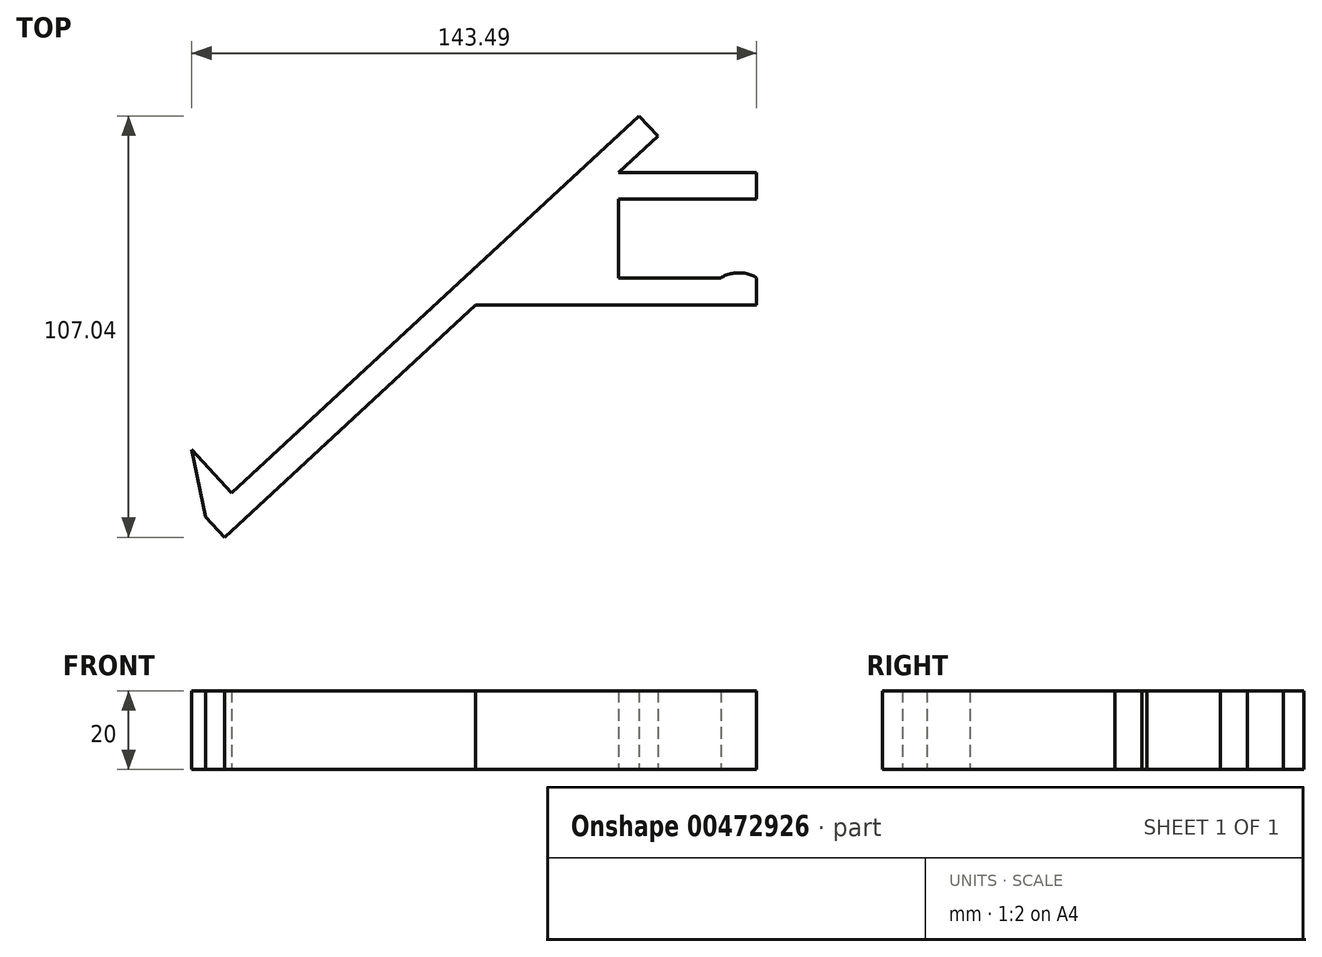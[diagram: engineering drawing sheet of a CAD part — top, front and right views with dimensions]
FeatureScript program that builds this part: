
annotation { "Feature Type Name" : "Feature", "Feature Type Description" : "" }
export const myFeature = defineFeature(function(context is Context, id is Id, definition is map)
    precondition{}
    {
        {
            var Q0;
            Q0=qCreatedBy(makeId("Top.planeOp"),FACE);
            var sketch = newSketch(context, id + "F0", { "sketchPlane" : qUnion([Q0])});
            skLineSegment(sketch, "E0.bottom", {"start": v(38.83, 15.84) * mm, "end": v(3.83, 15.84) * mm});
            skLineSegment(sketch, "E0.top", {"start": v(38.83, 9.02) * mm, "end": v(3.83, 9.02) * mm});
            skLineSegment(sketch, "E0.left", {"start": v(38.83, 15.84) * mm, "end": v(38.83, 9.02) * mm});
            skLineSegment(sketch, "E1.bottom", {"start": v(3.83, -10.98) * mm, "end": v(38.83, -10.98) * mm});
            skLineSegment(sketch, "E1.top", {"start": v(3.83, -17.8) * mm, "end": v(38.83, -17.8) * mm});
            skLineSegment(sketch, "E1.right", {"start": v(38.83, -10.98) * mm, "end": v(38.83, -17.8) * mm});
            skLineSegment(sketch, "E2.left", {"start": v(3.83, 9.02) * mm, "end": v(3.83, -10.98) * mm});
            skFitSpline(sketch, "E3", {"points": [v(29.8, -10.98) * mm, v(38.83, -10.98) * mm, v(41.23, -17.01) * mm], "startDerivative": vector(11.9, 8.99) * mm, "endDerivative": vector(2.49, -9.06) * mm});
            skLineSegment(sketch, "E4", {"start": v(13.75, 25.02) * mm, "end": v(3.83, 15.84) * mm});
            skLineSegment(sketch, "E5", {"start": v(3.83, -17.8) * mm, "end": v(-32.51, -17.8) * mm});
            skLineSegment(sketch, "E6", {"start": v(-96.32, -76.88) * mm, "end": v(-101.08, -71.74) * mm});
            skLineSegment(sketch, "E7", {"start": v(-94.47, -65.63) * mm, "end": v(9, 30.16) * mm});
            skLineSegment(sketch, "E8", {"start": v(9, 30.16) * mm, "end": v(13.75, 25.02) * mm});
            skLineSegment(sketch, "E9.trimOffspring", {"start": v(-32.51, -17.8) * mm, "end": v(-96.32, -76.88) * mm});
            skLineSegment(sketch, "E10", {"start": v(-101.08, -71.74) * mm, "end": v(-104.66, -54.62) * mm});
            skLineSegment(sketch, "E11", {"start": v(-104.66, -54.62) * mm, "end": v(-94.47, -65.63) * mm});
            skSolve(sketch);
        }
        {
            var Q0;
            Q0=qSketchRegion(id+"F0",true);
            extrude(context, id + "F1", {"entities" : qUnion([Q0]), "depth" : 20 * mm, "offsetDistance" : 25 * mm});
        }
    });
